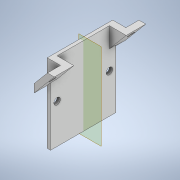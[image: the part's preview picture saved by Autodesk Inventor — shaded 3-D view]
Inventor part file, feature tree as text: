
AUTODESK INVENTOR PART (.ipt)
format: ipt  version: 2021 (Build 250183000, 183)  size: 157,184 bytes
history: native  units: in
note: dims shown in document units (in); Inventor stores cm internally (conversion verified against a paired STEP export)
features: sketch x5, extrude x3, hole x2, plane x1, mirror x1
ambient origin geometry x8: Origin, YZ Plane, XZ Plane, XY Plane, X Axis, Y Axis, Z Axis, Center Point
bodies: Solid1 (feature_tree)
feature tree (12):
  extrude  "Extrusion1"  Depth=2.5in
  hole  "Hole1"  [1 undecoded]
  extrude  "Extrusion2"  Depth=0.25in
  extrude  "Extrusion3"  Depth=0.5in
  plane  "Work Plane1"
  mirror  "Mirror1"
  hole  "Hole2"  [1 undecoded]
  sketch  "Sketch1"  dims[d0=3.0in d1=2.5in]
  sketch  "Sketch2"  dims[d2=0.125in d3=0.0in]
  sketch  "Sketch3"  dims[d4=0.25in d5=0.75in d6=0.375in d7=0.25in d8=0.5635in d9=1.0in d10=0.8108in d11=0.25in]
  sketch  "Sketch4"  dims[d12=0.25in d13=1.5in]
  sketch  "Sketch5"  dims[d14=1.5in d15=0.2749in d18=1.0in d19=0.25in d20=0.0in d21=0.2in d22=0.5in d23=0.0in d24=0.25in d25=0.75in d26=0.375in d27=0.25in d28=0.5635in d29=1.0in d30=0.8108in d31=3.0in d32=0.25in d33=0.5in]
note: 2 required parameter values undecoded (feature->parameter linkage not recoverable at this tier; creation-order binding heuristic only, values carry confidence <= 0.55)
